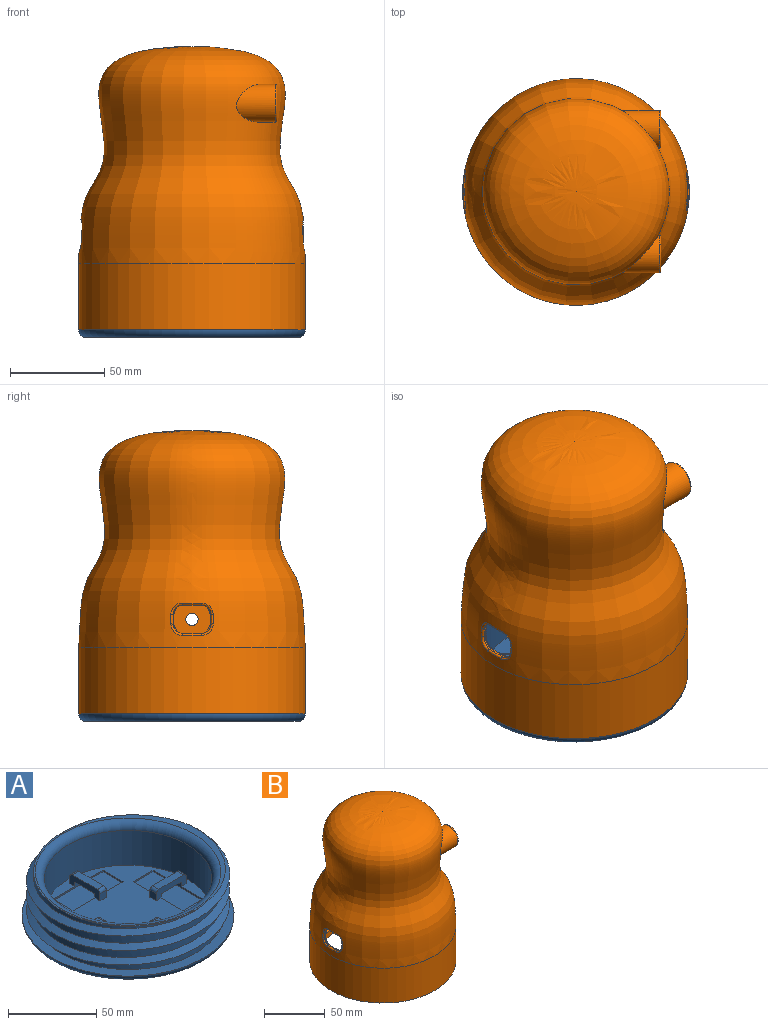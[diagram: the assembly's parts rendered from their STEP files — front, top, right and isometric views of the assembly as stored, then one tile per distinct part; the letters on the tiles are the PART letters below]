
ASSEMBLY  parts=2 mates=1
PART A: 62 faces, bbox 131.5x131.5x39.2 mm
  f0: plane 95x95mm, normal (0,0,1), area 4368.2mm2, adj f1,f2,f3,f4,f9,f14,f15,f16
  f1: plane 24x7mm, normal (1,0,0), area 118.3mm2, adj f0,f22,f23,f24,f48,f49,f51,f56
  f2: plane 24x7mm, normal (-1,0,0), area 118.3mm2, adj f0,f22,f23,f24,f48,f49,f51,f56
  f3: plane 24x7mm, normal (0,-1,0), area 118.3mm2, adj f0,f19,f20,f21,f30,f31,f33,f60
  f4: plane 24x7mm, normal (0,1,0), area 118.3mm2, adj f0,f19,f20,f21,f30,f31,f33,f60
  f5: bspline ~115x115mm, area 4833.4mm2, adj f6,f7,f8,f12
  f6: bspline ~115x115mm, area 4831.7mm2, adj f5,f7,f8,f12
  f7: cylinder r=53.5mm len=107mm, axis (0,0,-1), area 5517mm2, adj f5,f6,f8,f12
  f8: plane 112.38x108.72mm, normal (0,0,1), area 651.4mm2, adj f5,f6,f7,f10
  f9: cylinder r=47.5mm len=95mm, axis (0,0,1), area 7162.8mm2, adj f0,f10
  f10: torus R=52.5mm, axis (0,0,1), area 2433.7mm2, adj f8,f9
  f11: plane 112x112mm, normal (0,0,-1), area 9852mm2, adj f13
  f12: plane 121.64x121.64mm, normal (0,0,1), area 1999.3mm2, adj f5,f6,f7,f13
  f13: torus R=56mm, axis (0,0,1), area 2311.3mm2, adj f11,f12
  f14: plane 24x7mm, normal (0,-1,0), area 118.3mm2, adj f0,f15,f17,f18,f36,f38,f39,f58
  f15: plane 5x5mm, normal (1,0,0), area 25mm2, adj f0,f14,f16,f58
  f16: plane 24x7mm, normal (0,1,0), area 118.3mm2, adj f0,f15,f17,f18,f36,f38,f39,f58
  f17: plane 5x5mm, normal (-1,0,0), area 25mm2, adj f0,f14,f16,f59
  f18: plane 20x5mm, normal (0,0,1), area 100mm2, adj f14,f16,f58,f59
  f19: plane 5x5mm, normal (-1,0,0), area 25mm2, adj f0,f3,f4,f61
  f20: plane 5x5mm, normal (1,0,0), area 25mm2, adj f0,f3,f4,f60
  f21: plane 20x5mm, normal (0,0,1), area 100mm2, adj f3,f4,f60,f61
  f22: plane 5x5mm, normal (0,1,0), area 25mm2, adj f0,f1,f2,f56
  f23: plane 5x5mm, normal (0,-1,0), area 25mm2, adj f0,f1,f2,f57
  f24: plane 20x5mm, normal (0,0,1), area 100mm2, adj f1,f2,f56,f57
  f25: plane 24x7mm, normal (1,0,0), area 118.3mm2, adj f0,f26,f28,f29,f42,f44,f45,f54
  f26: plane 5x5mm, normal (0,1,0), area 25mm2, adj f0,f25,f27,f54
  f27: plane 24x7mm, normal (-1,0,0), area 118.3mm2, adj f0,f26,f28,f29,f42,f44,f45,f54
  f28: plane 5x5mm, normal (0,-1,0), area 25mm2, adj f0,f25,f27,f55
  f29: plane 20x5mm, normal (0,0,1), area 100mm2, adj f25,f27,f54,f55
  f30: plane 16x5mm, normal (0,0,-1), area 80mm2, adj f3,f4,f31,f33
  f31: plane 40x4mm, normal (1,0,0), area 55mm2, adj f0,f3,f4,f30,f32,f34,f35
  f32: plane 40x16mm, normal (0,0,1), area 640mm2, adj f31,f33,f34,f35
  f33: plane 40x4mm, normal (-1,0,0), area 55mm2, adj f0,f3,f4,f30,f32,f34,f35
  f34: plane 16x1mm, normal (0,-1,0), area 16mm2, adj f0,f31,f32,f33
  f35: plane 16x1mm, normal (0,1,0), area 16mm2, adj f0,f31,f32,f33
  f36: plane 16x5mm, normal (0,0,-1), area 80mm2, adj f14,f16,f38,f39
  f37: plane 40x16mm, normal (0,0,1), area 640mm2, adj f38,f39,f40,f41
  f38: plane 40x4mm, normal (-1,0,0), area 55mm2, adj f0,f14,f16,f36,f37,f40,f41
  f39: plane 40x4mm, normal (1,0,0), area 55mm2, adj f0,f14,f16,f36,f37,f40,f41
  f40: plane 16x1mm, normal (0,-1,0), area 16mm2, adj f0,f37,f38,f39
  f41: plane 16x1mm, normal (0,1,0), area 16mm2, adj f0,f37,f38,f39
  f42: plane 16x5mm, normal (0,0,-1), area 80mm2, adj f25,f27,f44,f45
  f43: plane 40x16mm, normal (0,0,1), area 640mm2, adj f44,f45,f46,f47
  f44: plane 40x4mm, normal (0,-1,0), area 55mm2, adj f0,f25,f27,f42,f43,f46,f47
  f45: plane 40x4mm, normal (0,1,0), area 55mm2, adj f0,f25,f27,f42,f43,f46,f47
  f46: plane 16x1mm, normal (1,0,0), area 16mm2, adj f0,f43,f44,f45
  f47: plane 16x1mm, normal (-1,0,0), area 16mm2, adj f0,f43,f44,f45
  f48: plane 16x5mm, normal (0,0,-1), area 80mm2, adj f1,f2,f49,f51
  f49: plane 40x4mm, normal (0,1,0), area 55mm2, adj f0,f1,f2,f48,f50,f52,f53
  f50: plane 40x16mm, normal (0,0,1), area 640mm2, adj f49,f51,f52,f53
  f51: plane 40x4mm, normal (0,-1,0), area 55mm2, adj f0,f1,f2,f48,f50,f52,f53
  f52: plane 16x1mm, normal (1,0,0), area 16mm2, adj f0,f49,f50,f51
  f53: plane 16x1mm, normal (-1,0,0), area 16mm2, adj f0,f49,f50,f51
  f54: cylinder r=2mm len=5mm, axis (1,0,0), area 15.7mm2, adj f25,f26,f27,f29
  f55: cylinder r=2mm len=5mm, axis (-1,0,0), area 15.7mm2, adj f25,f27,f28,f29
  f56: cylinder r=2mm len=5mm, axis (1,0,0), area 15.7mm2, adj f1,f2,f22,f24
  f57: cylinder r=2mm len=5mm, axis (-1,0,0), area 15.7mm2, adj f1,f2,f23,f24
  f58: cylinder r=2mm len=5mm, axis (0,-1,0), area 15.7mm2, adj f14,f15,f16,f18
  f59: cylinder r=2mm len=5mm, axis (0,1,0), area 15.7mm2, adj f14,f16,f17,f18
  f60: cylinder r=2mm len=5mm, axis (0,-1,0), area 15.7mm2, adj f3,f4,f20,f21
  f61: cylinder r=2mm len=5mm, axis (0,1,0), area 15.7mm2, adj f3,f4,f19,f21
PART B: 57 faces, bbox 121.7x121.7x135.9 mm
  f0: revolved ~113.84x113.73mm, area 298mm2, adj f1,f25,f26,f27,f28,f29,f30,f31
  f1: bspline ~7.28x7.22mm, area 11.8mm2, adj f0,f2,f25,f32
  f2: cylinder r=5mm len=5mm, axis (1,0,0), area 8mm2, adj f1,f3,f23,f24
  f3: plane 10x1.23mm, normal (0,0,1), area 10.1mm2, adj f2,f4,f22,f25
  f4: torus R=57.81mm, axis (0,0,-1), area 17mm2, adj f3,f5,f21,f24
  f5: revolved ~119.82x119.73mm, area 311.1mm2, adj f4,f6,f11,f12,f18,f19,f20,f21
  f6: bspline ~10.11x1.77mm, area 8.8mm2, adj f5,f7,f11,f21
  f7: plane 5x1.29mm, normal (0,1,0), area 5.1mm2, adj f6,f8,f22,f27
  f8: cylinder r=5mm len=5mm, axis (1,0,0), area 7.9mm2, adj f7,f9,f11,f28
  f9: plane 10x1.22mm, normal (0,0,-1), area 10mm2, adj f8,f10,f18,f30
  f10: cylinder r=5mm len=5mm, axis (1,0,0), area 7.9mm2, adj f9,f19,f23,f31
  f11: bspline ~7.45x7.34mm, area 14.1mm2, adj f5,f6,f8,f18
  f12: cylinder r=60mm len=120mm, axis (0,0,-1), area 13194.7mm2, adj f5,f13
  f13: plane 121.7x121.7mm, normal (0,0,1), area 1827.4mm2, adj f12,f14,f16,f17
  f14: bspline ~116x116mm, area 5132mm2, adj f13,f15,f16,f17
  f15: plane 4.62x4mm, normal (0,-1,0), area 9.2mm2, adj f14,f16,f17
  f16: bspline ~116x116mm, area 5499.3mm2, adj f13,f14,f15,f17
  f17: cylinder r=54mm len=108mm, axis (0,0,-1), area 6729mm2, adj f13,f14,f15,f16,f29
  f18: torus R=58.81mm, axis (0,0,-1), area 15.6mm2, adj f5,f9,f11,f19
  f19: bspline ~7.45x7.34mm, area 14.1mm2, adj f5,f10,f18,f20
  f20: bspline ~17.62x2.02mm, area 8.8mm2, adj f5,f19,f23,f24
  f21: bspline ~7.47x7.39mm, area 14.7mm2, adj f4,f5,f6,f22
  f22: cylinder r=5mm len=5mm, axis (1,0,0), area 8mm2, adj f3,f7,f21,f26
  f23: plane 5x1.29mm, normal (0,-1,0), area 5.1mm2, adj f2,f10,f20,f32
  f24: bspline ~7.47x7.39mm, area 14.7mm2, adj f2,f4,f5,f20
  f25: torus R=56.81mm, axis (0,0,-1), area 14.5mm2, adj f0,f1,f3,f26
  f26: bspline ~7.28x7.22mm, area 11.8mm2, adj f0,f22,f25,f27
  f27: bspline ~17.55x1.79mm, area 6.9mm2, adj f0,f7,f26,f28
  f28: bspline ~7.31x7.2mm, area 12.6mm2, adj f0,f8,f27,f30
  f29: plane 114x114mm, normal (0,0,-1), area 1045.7mm2, adj f0,f17
  f30: torus R=57.8mm, axis (0,0,-1), area 15.9mm2, adj f0,f9,f28,f31
  f31: bspline ~7.31x7.2mm, area 12.6mm2, adj f0,f10,f30,f32
  f32: bspline ~17.55x1.79mm, area 6.9mm2, adj f0,f1,f23,f31
  f33: revolved ~15.85x14.75mm, area 228.1mm2, adj f34
  f34: cylinder r=7mm len=18.17mm, axis (1,0,0), area 436.8mm2, adj f33,f35
  f35: plane 14x14mm, normal (1,0,0), area 120.8mm2, adj f34,f36
  f36: cylinder r=3.25mm len=6.5mm, axis (1,0,0), area 81.7mm2, adj f35,f37
  f37: plane 18x18mm, normal (-1,0,0), area 221.3mm2, adj f36,f38
  f38: torus R=9mm, axis (1,0,0), area 95.1mm2, adj f37,f39
  f39: cylinder r=10mm len=20.39mm, axis (1,0,0), area 600.2mm2, adj f38,f40
  f40: revolved ~20.86x20.58mm, area 444.9mm2, adj f39
  f41: revolved ~15.85x14.75mm, area 228.3mm2, adj f42
  f42: cylinder r=7mm len=18.17mm, axis (1,0,0), area 436.9mm2, adj f41,f43
  f43: plane 14x14mm, normal (1,0,0), area 120.8mm2, adj f42,f44
  f44: cylinder r=3.25mm len=6.5mm, axis (1,0,0), area 81.7mm2, adj f43,f45
  f45: plane 18x18mm, normal (-1,0,0), area 221.3mm2, adj f44,f46
  f46: torus R=9mm, axis (1,0,0), area 95.1mm2, adj f45,f47
  f47: cylinder r=10mm len=20.39mm, axis (1,0,0), area 600.2mm2, adj f46,f48
  f48: revolved ~20.86x20.58mm, area 444.7mm2, adj f47
  f49: revolved ~20.14x20mm, area 315.9mm2, adj f50
  f50: cylinder r=10mm len=20mm, axis (1,0,0), area 56.7mm2, adj f49,f51
  f51: plane 20x20mm, normal (1,0,0), area 281mm2, adj f50,f52
  f52: cylinder r=3.25mm len=6.5mm, axis (1,0,0), area 81.7mm2, adj f51,f53
  f53: plane 20x20mm, normal (-1,0,0), area 281mm2, adj f52,f54,f56
  f54: cylinder r=10mm len=20mm, axis (1,0,0), area 0mm2, adj f53,f55
  f55: revolved ~20.14x20mm, area 315.9mm2, adj f54,f56
  f56: cylinder r=10mm len=17.76mm, axis (-1,0,0), area 0mm2, adj f53,f55
PLACE A rot(axis=(0,0,1),49.8deg) t=(0.23,-0.22,-197.08)mm
PLACE B t=(0.23,-0.22,-197)mm fixed
MATE cylindrical B.f17 <-> A.f9  axis (0,0,1) through (0.23,-0.22,-162)mm
